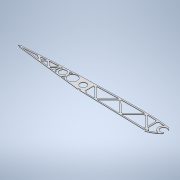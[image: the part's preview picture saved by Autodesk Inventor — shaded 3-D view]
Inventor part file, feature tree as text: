
AUTODESK INVENTOR PART (.ipt)
format: ipt  version: 2022 (Build 260153000, 153)  size: 451,072 bytes
history: native  units: mm
features: extrude x1, sketch x1
ambient origin geometry x8: Origin, YZ Plane, XZ Plane, XY Plane, X Axis, Y Axis, Z Axis, Center Point
bodies: Body1 (feature_tree)
feature tree (2):
  extrude  "Extrusion5"  Depth=10.0mm
  sketch  "Sketch1"  dims[d31=34.456mm d50=368.759386mm d57=16.0mm d69=8.0mm d70=23.0mm d71=8.0mm d73=16.0mm d80=19.0mm d81=16.0mm d82=1.0mm d83=1.0mm d84=1.0mm d85=1.0mm d86=1.0mm d87=0.8mm d88=1.0mm d90=19.0mm d94=5.0mm d95=5.0mm d105=5.0mm d106=5.0mm d108=2.0mm d109=19.0mm d114=5.0mm d115=5.0mm d116=24.0mm d117=2.5mm d118=2.5mm d123=2.5mm d124=2.5mm d125=10.0mm d126=24.0mm d127=24.0mm d128=27.0mm d135=0.5mm d136=45.0deg d139=7.0mm d165=45.0deg d169=27.0mm d175=90.0deg d181=45.0deg d185=7.0mm d186=45.0deg d190=7.0mm d191=45.0deg d197=90.0deg d203=90.0deg d206=7.0mm d207=1.0mm d208=0.0mm]
